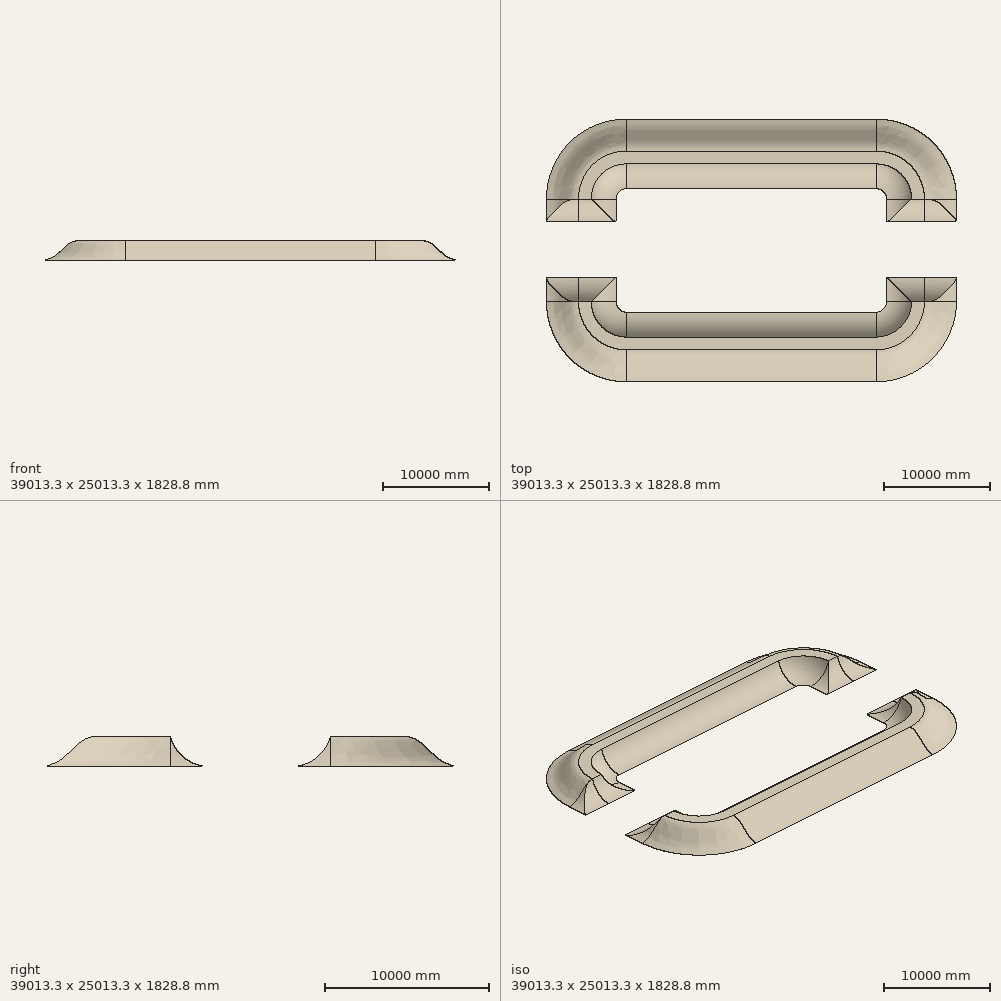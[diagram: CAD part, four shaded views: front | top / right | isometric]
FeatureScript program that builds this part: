
annotation { "Feature Type Name" : "Feature", "Feature Type Description" : "" }
export const myFeature = defineFeature(function(context is Context, id is Id, definition is map)
    precondition{}
    {
        {
            var Q0;
            Q0=qCreatedBy(makeId("Top.planeOp"),FACE);
            var sketch = newSketch(context, id + "F0", { "sketchPlane" : qUnion([Q0])});
            skLineSegment(sketch, "E0.bottom", {"start": v(16000, 9000) * mm, "end": v(-16000, 9000) * mm});
            skLineSegment(sketch, "E0.top", {"start": v(16000, -9000) * mm, "end": v(-16000, -9000) * mm});
            skLineSegment(sketch, "E0.left", {"start": v(16000, 9000) * mm, "end": v(16000, -9000) * mm});
            skLineSegment(sketch, "E0.right", {"start": v(-16000, 9000) * mm, "end": v(-16000, -9000) * mm});
            skPoint(sketch, "E0.middle", {"position": v(0, 0) * mm});
            skLineSegment(sketch, "E1.bottom", {"start": v(13780.8, 7780.8) * mm, "end": v(-13780.8, 7780.8) * mm});
            skLineSegment(sketch, "E1.top", {"start": v(13780.8, -7780.8) * mm, "end": v(-13780.8, -7780.8) * mm});
            skLineSegment(sketch, "E1.left", {"start": v(14780.8, 6780.8) * mm, "end": v(14780.8, -6780.8) * mm});
            skLineSegment(sketch, "E1.right", {"start": v(-14780.8, 6780.8) * mm, "end": v(-14780.8, -6780.8) * mm});
            skPoint(sketch, "E2.visualSharp", {"position": v(-14780.8, 7780.8) * mm});
            skArc(sketch, "E2.filletArc", {"start": v(-13780.8, 7780.8) * mm, "mid": v(-14487.9, 7487.9) * mm, "end": v(-14780.8, 6780.8) * mm});
            skPoint(sketch, "E3.visualSharp", {"position": v(14780.8, 7780.8) * mm});
            skArc(sketch, "E3.filletArc", {"start": v(14780.8, 6780.8) * mm, "mid": v(14487.9, 7487.9) * mm, "end": v(13780.8, 7780.8) * mm});
            skPoint(sketch, "E4.visualSharp", {"position": v(14780.8, -7780.8) * mm});
            skArc(sketch, "E4.filletArc", {"start": v(13780.8, -7780.8) * mm, "mid": v(14487.9, -7487.9) * mm, "end": v(14780.8, -6780.8) * mm});
            skPoint(sketch, "E5.visualSharp", {"position": v(-14780.8, -7780.8) * mm});
            skArc(sketch, "E5.filletArc", {"start": v(-14780.8, -6780.8) * mm, "mid": v(-14487.9, -7487.9) * mm, "end": v(-13780.8, -7780.8) * mm});
            skLineSegment(sketch, "E6.0", {"start": v(11880.8, 5880.8) * mm, "end": v(-11880.8, 5880.8) * mm});
            skLineSegment(sketch, "E6.1", {"start": v(12880.8, 4880.8) * mm, "end": v(12880.8, -4880.8) * mm});
            skLineSegment(sketch, "E6.2", {"start": v(11880.8, -5880.8) * mm, "end": v(-11880.8, -5880.8) * mm});
            skLineSegment(sketch, "E6.3", {"start": v(-12880.8, 4880.8) * mm, "end": v(-12880.8, -4880.8) * mm});
            skPoint(sketch, "E7.visualSharp", {"position": v(-12880.8, 5880.8) * mm});
            skArc(sketch, "E7.filletArc", {"start": v(-11880.8, 5880.8) * mm, "mid": v(-12587.9, 5587.9) * mm, "end": v(-12880.8, 4880.8) * mm});
            skPoint(sketch, "E8.visualSharp", {"position": v(12880.8, 5880.8) * mm});
            skArc(sketch, "E8.filletArc", {"start": v(12880.8, 4880.8) * mm, "mid": v(12587.9, 5587.9) * mm, "end": v(11880.8, 5880.8) * mm});
            skPoint(sketch, "E9.visualSharp", {"position": v(12880.8, -5880.8) * mm});
            skArc(sketch, "E9.filletArc", {"start": v(11880.8, -5880.8) * mm, "mid": v(12587.9, -5587.9) * mm, "end": v(12880.8, -4880.8) * mm});
            skPoint(sketch, "E10.visualSharp", {"position": v(-12880.8, -5880.8) * mm});
            skArc(sketch, "E10.filletArc", {"start": v(-12880.8, -4880.8) * mm, "mid": v(-12587.9, -5587.9) * mm, "end": v(-11880.8, -5880.8) * mm});
            skSolve(sketch);
        }
        {
            var Q0;
            Q0=sQuery(id+"F0.wireOp",EDGE,"E1.right");
            cPoint(context, id + "F1", {"entities" : qUnion([Q0]), "parameter" : 0.5});
        }
        {
            var Q0;
            Q0=sQuery(id+"F0.wireOp",EDGE,"E1.right");
            var Q1;
            Q1 = qCreatedBy(id + "F1" ,VERTEX);
            cPlane(context, id + "F2", {"entities" : qUnion([Q0, Q1]), "cplaneType" : CPlaneType.LINE_POINT, "offset" : 25 * mm, "width" : 150 * mm, "height" : 150 * mm});
        }
        {
            var Q0;
            Q0=qCreatedBy(id+"F2.planeOp",FACE);
            var sketch = newSketch(context, id + "F3", { "sketchPlane" : qUnion([Q0])});
            skLineSegment(sketch, "E11", {"start": v(-15239.45, 0) * mm, "end": v(-15239.45, 1828.8) * mm});
            skLineSegment(sketch, "E12", {"start": v(-15239.45, 0) * mm, "end": v(-11799.49, 0) * mm});
            skLineSegment(sketch, "E13", {"start": v(-14972.73, 2438.4) * mm, "end": v(-11717.25, 2438.4) * mm, "construction": true});
            skArc(sketch, "E14", {"start": v(-15239.45, 1828.8) * mm, "mid": v(-14371.69, 510.68) * mm, "end": v(-12878.48, 0) * mm});
            skLineSegment(sketch, "E15", {"start": v(-15239.45, 1828.8) * mm, "end": v(-15433.7, 1828.8) * mm, "construction": true});
            skLineSegment(sketch, "E16", {"start": v(-15239.45, 1828.8) * mm, "end": v(-15223.93, 1367.02) * mm, "construction": true});
            skPoint(sketch, "E17.0", {"position": v(-15239.45, 0) * mm});
            skLineSegment(sketch, "E18", {"start": v(-15239.45, 0) * mm, "end": v(-16458.65, 0) * mm});
            skLineSegment(sketch, "E19", {"start": v(-16458.65, 0) * mm, "end": v(-16458.65, 1828.8) * mm});
            skLineSegment(sketch, "E20", {"start": v(-16458.65, 1828.8) * mm, "end": v(-15239.45, 1828.8) * mm});
            skLineSegment(sketch, "E21", {"start": v(-16458.65, 0) * mm, "end": v(-19506.65, 0) * mm});
            skFitSpline(sketch, "E22", {"points": [v(-16458.65, 1828.8) * mm, v(-17643.92, 1227.21) * mm, v(-18526.83, 422.78) * mm, v(-19506.65, 0) * mm], "startDerivative": vector(-4054.5, -28.6) * mm, "endDerivative": vector(-3314.4, -952.64) * mm});
            skSolve(sketch);
        }
        {
            var Q0;
            {var subQ0=sQuery(id+"F3.wireOp",EDGE,"E11");Q0=makeQuery(id+"F3.imprint","IMPRINT",FACE,{"disambiguationData":[TD([[makeQuery(id+"F3.imprint","IMPRINT",EDGE,{"derivedFrom":subQ0}),-1.0]])]});}
            var Q1;
            Q1=makeQuery(id+"F3.imprint","IMPRINT",FACE,{"disambiguationData":[TD([[makeQuery(id+"F3.imprint","IMPRINT",EDGE,{"derivedFrom":sQuery(id+"F3.wireOp",EDGE,"E11")}),1.0]])]});
            var Q2;
            Q2=sQuery(id+"F0.wireOp",EDGE,"E6.3");
            var Q3;
            Q3=sQuery(id+"F0.wireOp",EDGE,"E10.filletArc");
            var Q4;
            Q4=sQuery(id+"F0.wireOp",EDGE,"E6.2");
            var Q5;
            Q5=sQuery(id+"F0.wireOp",EDGE,"E7.filletArc");
            var Q6;
            Q6=sQuery(id+"F0.wireOp",EDGE,"E6.0");
            var Q7;
            Q7=sQuery(id+"F0.wireOp",EDGE,"E8.filletArc");
            var Q8;
            Q8=sQuery(id+"F0.wireOp",EDGE,"E6.1");
            var Q9;
            Q9=sQuery(id+"F0.wireOp",EDGE,"E9.filletArc");
            sweep(context, id + "F4", {"profiles" : qUnion([Q0, Q1]), "path" : qUnion([Q2, Q3, Q4, Q5, Q6, Q7, Q8, Q9])});
        }
        {
            var Q0;
            Q0=makeQuery(id+"F3.imprint","IMPRINT",FACE,{"disambiguationData":[TD([[makeQuery(id+"F3.imprint","IMPRINT",EDGE,{"derivedFrom":sQuery(id+"F3.wireOp",EDGE,"E19")}),1.0]])]});
            var Q1;
            Q1=makeQuery(id+"F4.opSweep","SWEPT_EDGE",EDGE,{"disambiguationData":[OSD([sQuery(id+"F0.wireOp",EDGE,"E6.2"),sQuery(id+"F3.wireOp",EDGE,"E18"),sQuery(id+"F3.wireOp",EDGE,"E19"),sQuery(id+"F3.wireOp",EDGE,"E21")])]});
            var Q2;
            Q2=makeQuery(id+"F4.opSweep","SWEPT_EDGE",EDGE,{"disambiguationData":[OSD([sQuery(id+"F0.wireOp",EDGE,"E10.filletArc"),sQuery(id+"F3.wireOp",EDGE,"E18"),sQuery(id+"F3.wireOp",EDGE,"E19"),sQuery(id+"F3.wireOp",EDGE,"E21")])]});
            var Q3;
            Q3=makeQuery(id+"F4.opSweep","SWEPT_EDGE",EDGE,{"disambiguationData":[OSD([sQuery(id+"F0.wireOp",EDGE,"E7.filletArc"),sQuery(id+"F3.wireOp",EDGE,"E18"),sQuery(id+"F3.wireOp",EDGE,"E19"),sQuery(id+"F3.wireOp",EDGE,"E21")])]});
            var Q4;
            Q4=makeQuery(id+"F4.opSweep","SWEPT_EDGE",EDGE,{"disambiguationData":[OSD([sQuery(id+"F0.wireOp",EDGE,"E6.0"),sQuery(id+"F3.wireOp",EDGE,"E18"),sQuery(id+"F3.wireOp",EDGE,"E19"),sQuery(id+"F3.wireOp",EDGE,"E21")])]});
            var Q5;
            Q5=makeQuery(id+"F4.opSweep","SWEPT_EDGE",EDGE,{"disambiguationData":[OSD([sQuery(id+"F0.wireOp",EDGE,"E8.filletArc"),sQuery(id+"F3.wireOp",EDGE,"E18"),sQuery(id+"F3.wireOp",EDGE,"E19"),sQuery(id+"F3.wireOp",EDGE,"E21")])]});
            var Q6;
            Q6=makeQuery(id+"F4.opSweep","SWEPT_EDGE",EDGE,{"disambiguationData":[OSD([sQuery(id+"F0.wireOp",EDGE,"E6.1"),sQuery(id+"F3.wireOp",EDGE,"E18"),sQuery(id+"F3.wireOp",EDGE,"E19"),sQuery(id+"F3.wireOp",EDGE,"E21")])]});
            var Q7;
            Q7=makeQuery(id+"F4.opSweep","SWEPT_EDGE",EDGE,{"disambiguationData":[OSD([sQuery(id+"F0.wireOp",EDGE,"E9.filletArc"),sQuery(id+"F3.wireOp",EDGE,"E18"),sQuery(id+"F3.wireOp",EDGE,"E19"),sQuery(id+"F3.wireOp",EDGE,"E21")])]});
            var Q8;
            Q8=makeQuery(id+"F4.opSweep","SWEPT_EDGE",EDGE,{"disambiguationData":[OSD([sQuery(id+"F0.wireOp",EDGE,"E6.3"),sQuery(id+"F3.wireOp",EDGE,"E18"),sQuery(id+"F3.wireOp",EDGE,"E19"),sQuery(id+"F3.wireOp",EDGE,"E21")])]});
            sweep(context, id + "F5", {"profiles" : qUnion([Q0]), "path" : qUnion([Q1, Q2, Q3, Q4, Q5, Q6, Q7, Q8])});
        }
        {
            var Q0;
            Q0=makeQuery(id+"F4.opSweep","SWEPT_FACE",FACE,{"disambiguationData":[OSD([sQuery(id+"F0.wireOp",EDGE,"E6.1"),sQuery(id+"F3.wireOp",EDGE,"E19")])]});
            var sketch = newSketch(context, id + "F6", { "sketchPlane" : qUnion([Q0])});
            skLineSegment(sketch, "E23.0", {"start": v(-4880.8, 0) * mm, "end": v(4880.8, 0) * mm});
            skLineSegment(sketch, "E24.0", {"start": v(-4880.8, 1828.8) * mm, "end": v(4880.8, 1828.8) * mm});
            skLineSegment(sketch, "E24.1", {"start": v(4880.8, 1828.8) * mm, "end": v(4880.8, 0) * mm});
            skLineSegment(sketch, "E24.2", {"start": v(-4880.8, 1828.8) * mm, "end": v(-4880.8, 0) * mm});
            skLineSegment(sketch, "E25", {"start": v(-4863.6, 2438.4) * mm, "end": v(6324.1, 2438.4) * mm, "construction": true});
            skArc(sketch, "E26", {"start": v(-4880.8, 1828.8) * mm, "mid": v(-3974.87, 480.38) * mm, "end": v(-2423.05, 0) * mm});
            skArc(sketch, "E27", {"start": v(2322.43, 0) * mm, "mid": v(3937.89, 443.98) * mm, "end": v(4880.8, 1828.8) * mm});
            skSolve(sketch);
        }
        {
            var Q0;
            {var subQ0=sQuery(id+"F6.wireOp",EDGE,"E24.0");Q0=makeQuery(id+"F6.imprint","IMPRINT",FACE,{"disambiguationData":[TD([[makeQuery(id+"F6.imprint","IMPRINT",EDGE,{"derivedFrom":subQ0}),-1.0]])]});}
            extrude(context, id + "F7", {"entities" : qUnion([Q0]), "operationType" : NewBodyOperationType.REMOVE, "endBound" : BoundingType.THROUGH_ALL, "oppositeDirection" : true, "depth" : 25 * mm, "offsetDistance" : 25 * mm});
        }
        {
            var Q0;
            Q0=makeQuery(id+"F5.opSweep","SWEPT_FACE",FACE,{"disambiguationData":[OSD([sQuery(id+"F0.wireOp",EDGE,"E6.1"),sQuery(id+"F3.wireOp",EDGE,"E18"),sQuery(id+"F3.wireOp",EDGE,"E19"),sQuery(id+"F3.wireOp",EDGE,"E21")])]});
            var sketch = newSketch(context, id + "F8", { "sketchPlane" : qUnion([Q0])});
            skLineSegment(sketch, "E28.0", {"start": v(4880.8, 1828.8) * mm, "end": v(-4880.8, 1828.8) * mm});
            skArc(sketch, "E28.1", {"start": v(4880.8, 1828.8) * mm, "mid": v(4050.63, 539.1) * mm, "end": v(2614.71, 0) * mm});
            skArc(sketch, "E28.2", {"start": v(-2730.62, 0) * mm, "mid": v(-4098.93, 569.66) * mm, "end": v(-4880.8, 1828.8) * mm});
            skLineSegment(sketch, "E28.3", {"start": v(4880.8, 0) * mm, "end": v(-4880.8, 0) * mm});
            skSolve(sketch);
        }
        {
            var Q0;
            Q0=makeQuery(id+"F8.imprint","IMPRINT",FACE,{"disambiguationData":[TD([[makeQuery(id+"F8.imprint","IMPRINT",EDGE,{"derivedFrom":sQuery(id+"F8.wireOp",EDGE,"E28.0")}),1.0]])]});
            extrude(context, id + "F9", {"entities" : qUnion([Q0]), "operationType" : NewBodyOperationType.REMOVE, "endBound" : BoundingType.THROUGH_ALL, "depth" : 25 * mm, "offsetDistance" : 25 * mm, "hasSecondDirection" : true, "secondDirectionBound" : BoundingType.THROUGH_ALL, "secondDirectionOppositeDirection" : true, "secondDirectionDepth" : 25 * mm});
        }
    });
